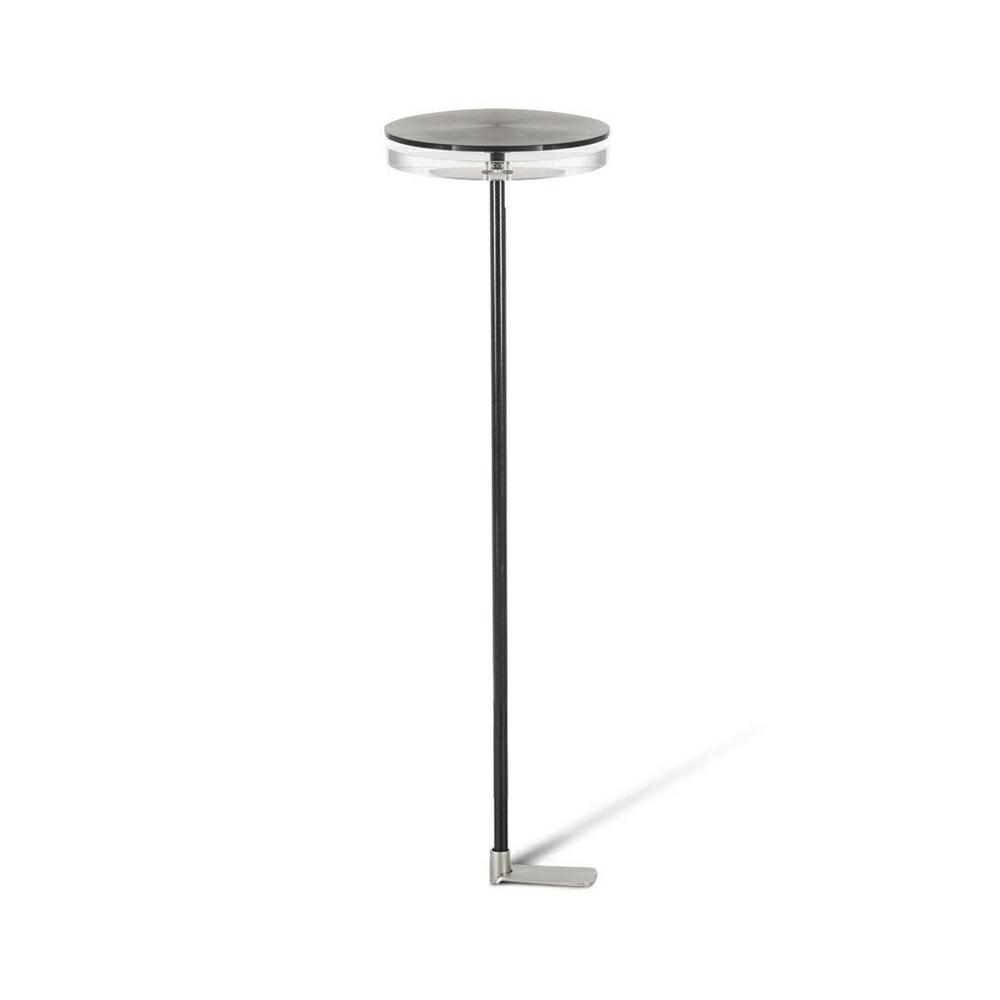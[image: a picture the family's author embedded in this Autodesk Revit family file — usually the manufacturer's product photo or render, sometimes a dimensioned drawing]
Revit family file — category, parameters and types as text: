
# Revit family: Platek_Chiodo Bollard
name_source: partatom
category: Apparecchi per illuminazione
revit_build: Autodesk Revit 2017 (Build: 20160225_1515(x64)
units: mm (PartAtom-declared; Revit-internal decimal feet)

## family parameters
Basato su piano di lavoro = No
Condiviso = No
Punto di calcolo locali = No
Quota connettore circolare = Usa diametro
Sempre verticale = Sì
Sorgente d'illuminazione = Sì
Taglio con vuoti quando caricato = No
Tipo di parte = Normale

## types (3) — shared parameters
Aluminium = PLK_Aluminium
Angolo inclinazione = 90.00°
Beam Angle = 95.00°
Body = PLK_Black
CRI = >80
Carico apparente = 0 VA
Codice assieme = 9402116.01 (Black)
Colour Temperature = 3000 K
Commenti sul tipo = Suitable for bushes, flower beds, paths, grass
Descrizione = Outdoor Lighting, ground mounted, garden product
Diffuse Type = Polycarbonate
Dimmable = No
Emetti da diametro cerchio = 180 mm  [stored 0.590551 ft]
Energy Efficiency Rating = A/A+/A++
Filtro dei colori = 16777215
Frequency = 50/60 Hz
IK Rating = IK 05
IP Rating = IP65
Insulation Class = 1
LED Protection = Surge protection included
Lampada = LED
Light Source = PLK_Light Source
Luminaire Luminous Flux = 660 lm
Luminaire Luminous Intensity = 248 cd
Luminaire Wattage = 12 W
Manufacturer Comment = IP68 Connector excluded to be ordered separately
Modello = Chiodo Bollard
Mounting Type = Ground
Nota chiave = Plate could fixing on floor; Other Led colors available on request
PLATEK FInishes = Avalaible in black
Part of body = PLK_Part of body
Pole = PLK_Pole
Power Supply Unit = Included
Product Documentation Link = http://www.platek.eu
Product Page URL = http://www.platek.eu
Produttore = PLATEK SRL
Rendi la forma visibile nel rendering = No
Supply Voltage = 230 V
Supply Voltage Max = 230 V
Supply Voltage Min = 220 V
URL = www.platek.eu
Variazione temperatura colore lampada con luminosità attenuata = <Nessuno>

## per-type parameters (varying)
| type | Cable Lenght | File diagramma fotometrico | H1100 | H1700 | H600 | Height | Immagine tipo | PLATEK Article Code | Product Dimension |
| 9402116_12.1W_LED_3000K_H600mm | 4,4 (3x1 mm^2) | 9402116.ies | No | No | Sì | 600 mm  [stored 1.9685 ft] | chiodo_600.jpg | 9402116 | D180mm x H600mm |
| 9402216_12.1W_LED_3000K_H1100mm | 3,9 (3x1 mm^2) | 9402216.ies | Sì | No | No | 1100 mm | chiodo_1100.jpg | 9402216 | D180mm x H1100mm |
| 9402316_12.1W_LED_3000K_H1700mm | 3,3 (3x1 mm^2) | 9402316.ies | No | Sì | No | 1700 mm  [stored 5.57743 ft] | chiodo_1700.jpg | 9402316 | D180mm x H1700mm |

note: [stored X ft] marks values corroborated as IEEE doubles in the binary element streams (Revit-internal decimal feet)
